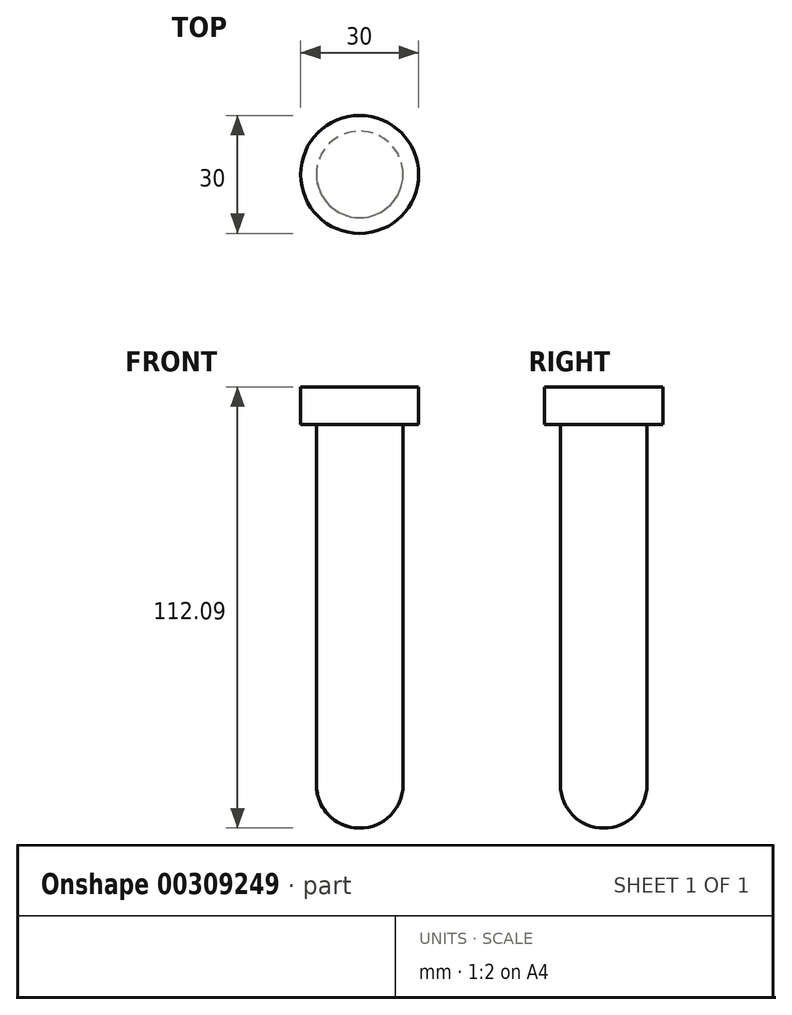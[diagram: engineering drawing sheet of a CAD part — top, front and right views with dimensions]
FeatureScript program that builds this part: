
annotation { "Feature Type Name" : "Feature", "Feature Type Description" : "" }
export const myFeature = defineFeature(function(context is Context, id is Id, definition is map)
    precondition{}
    {
        {
            var Q0;
            Q0=qCreatedBy(makeId("Front.planeOp"),FACE);
            var sketch = newSketch(context, id + "F0", { "sketchPlane" : qUnion([Q0])});
            skArc(sketch, "E0", {"start": v(0, -46.6) * mm, "mid": v(7.78, -43.39) * mm, "end": v(11, -35.6) * mm});
            skLineSegment(sketch, "E1", {"start": v(0, 65.48) * mm, "end": v(11, 65.48) * mm});
            skLineSegment(sketch, "E2", {"start": v(11, 65.48) * mm, "end": v(11, -35.6) * mm});
            skLineSegment(sketch, "E3", {"start": v(0, 65.48) * mm, "end": v(0, -46.6) * mm});
            skSolve(sketch);
        }
        {
            var Q0;
            Q0=makeQuery(id+"F0.imprint","IMPRINT",FACE,{"disambiguationData":[TD([[makeQuery(id+"F0.imprint","IMPRINT",EDGE,{"derivedFrom":sQuery(id+"F0.wireOp",EDGE,"E0")}),1.0]])]});
            var Q1;
            Q1=sQuery(id+"F0.wireOp",EDGE,"E3");
            revolve(context, id + "F1", {"entities" : qUnion([Q0]), "axis" : qUnion([Q1]), "revolveType" : RevolveType.FULL});
        }
        {
            var Q0;
            Q0=makeQuery(id+"F1.opRevolve","SWEPT_FACE",FACE,{"disambiguationData":[OSD([sQuery(id+"F0.wireOp",EDGE,"E1")])]});
            var sketch = newSketch(context, id + "F2", { "sketchPlane" : qUnion([Q0])});
            skCircle(sketch, "E4", {"center": v(0, 0) * mm, "radius": 15 * mm});
            skSolve(sketch);
        }
        {
            var Q0;
            Q0=makeQuery(id+"F2.imprint","IMPRINT",FACE,{"disambiguationData":[TD([[makeQuery(id+"F2.imprint","IMPRINT",EDGE,{"derivedFrom":sQuery(id+"F2.wireOp",EDGE,"E4")}),1.0]])]});
            extrude(context, id + "F3", {"entities" : qUnion([Q0]), "operationType" : NewBodyOperationType.ADD, "oppositeDirection" : true, "depth" : 9.5 * mm});
        }
    });
